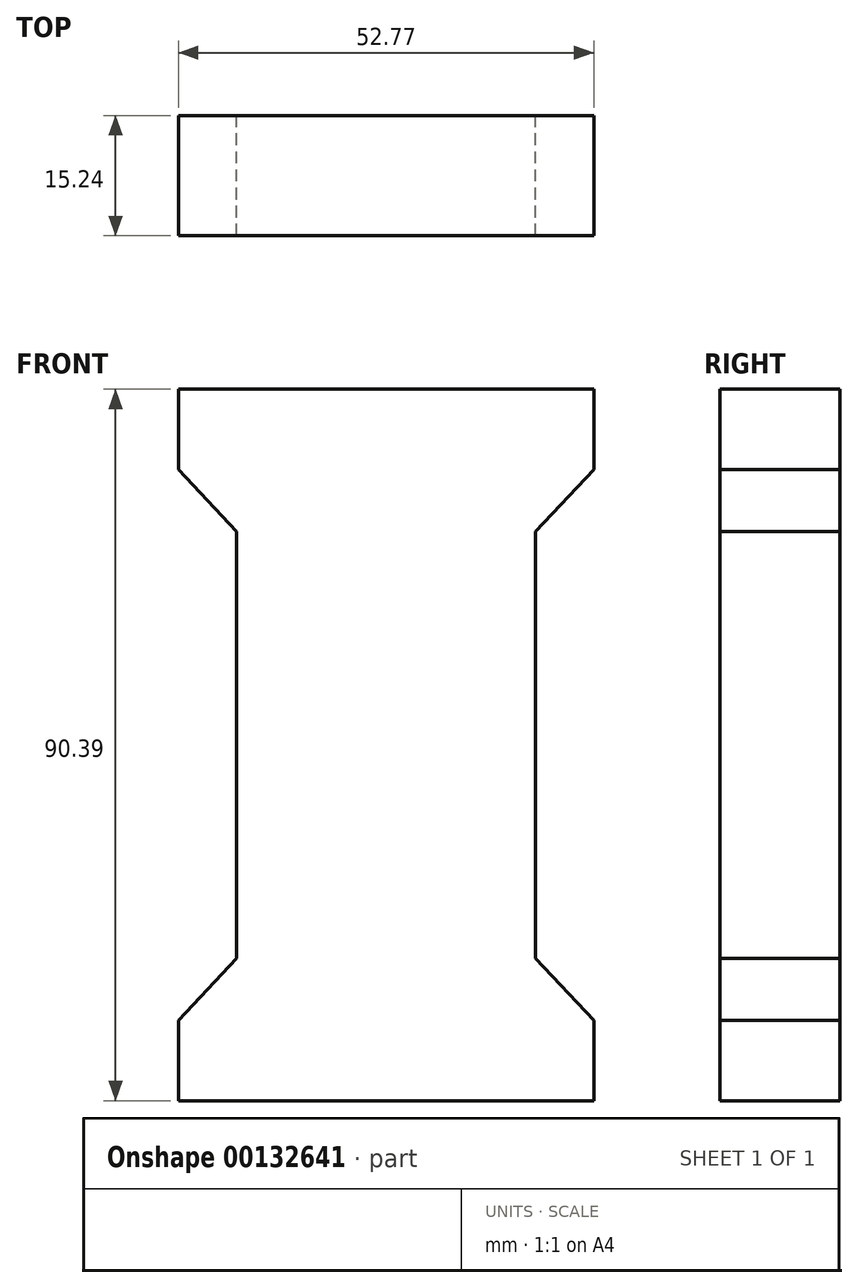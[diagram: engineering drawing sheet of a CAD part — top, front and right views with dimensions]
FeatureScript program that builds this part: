
annotation { "Feature Type Name" : "Feature", "Feature Type Description" : "" }
export const myFeature = defineFeature(function(context is Context, id is Id, definition is map)
    precondition{}
    {
        {
            var Q0;
            Q0=qCreatedBy(makeId("Front.planeOp"),FACE);
            var sketch = newSketch(context, id + "F0", { "sketchPlane" : qUnion([Q0])});
            skLineSegment(sketch, "E0.bottom", {"start": v(25.83, -45.47) * mm, "end": v(-26.94, -45.47) * mm});
            skLineSegment(sketch, "E0.top", {"start": v(25.83, 44.92) * mm, "end": v(-26.94, 44.92) * mm});
            skLineSegment(sketch, "E0.left", {"start": v(25.83, -45.47) * mm, "end": v(25.83, -35.25) * mm});
            skLineSegment(sketch, "E0.right", {"start": v(-26.94, -45.47) * mm, "end": v(-26.94, -35.25) * mm});
            skPoint(sketch, "E0.middle", {"position": v(-0.55, -0.28) * mm});
            skLineSegment(sketch, "E1.left", {"start": v(18.43, -27.37) * mm, "end": v(18.43, 26.81) * mm});
            skLineSegment(sketch, "E1.right", {"start": v(-19.54, -27.37) * mm, "end": v(-19.54, 26.81) * mm});
            skLineSegment(sketch, "E2", {"start": v(25.83, -35.25) * mm, "end": v(18.43, -27.37) * mm});
            skLineSegment(sketch, "E3.MirrorCS", {"start": v(-26.94, -35.25) * mm, "end": v(-19.54, -27.37) * mm});
            skLineSegment(sketch, "E4.MirrorCS", {"start": v(25.83, 34.7) * mm, "end": v(18.43, 26.81) * mm});
            skLineSegment(sketch, "E5.MirrorCS", {"start": v(-26.94, 34.7) * mm, "end": v(-19.54, 26.81) * mm});
            skLineSegment(sketch, "E6.trimOffspring", {"start": v(25.83, 34.7) * mm, "end": v(25.83, 44.92) * mm});
            skPoint(sketch, "E1.bottom.start.orphan", {"position": v(18.43, -32.96) * mm});
            skPoint(sketch, "E7.orphan", {"position": v(-19.54, -32.96) * mm});
            skPoint(sketch, "E1.top.start.orphan", {"position": v(18.43, 32.4) * mm});
            skPoint(sketch, "E8.orphan", {"position": v(-19.54, 32.4) * mm});
            skLineSegment(sketch, "E9.trimOffspring", {"start": v(-26.94, 34.7) * mm, "end": v(-26.94, 44.92) * mm});
            skSolve(sketch);
        }
        {
            var Q0;
            Q0=makeQuery(id+"F0.imprint","IMPRINT",FACE,{"disambiguationData":[TD([[makeQuery(id+"F0.imprint","IMPRINT",EDGE,{"derivedFrom":sQuery(id+"F0.wireOp",EDGE,"E0.bottom")}),-1.0]])]});
            extrude(context, id + "F1", {"entities" : qUnion([Q0]), "depth" : 15.24 * mm});
        }
    });
